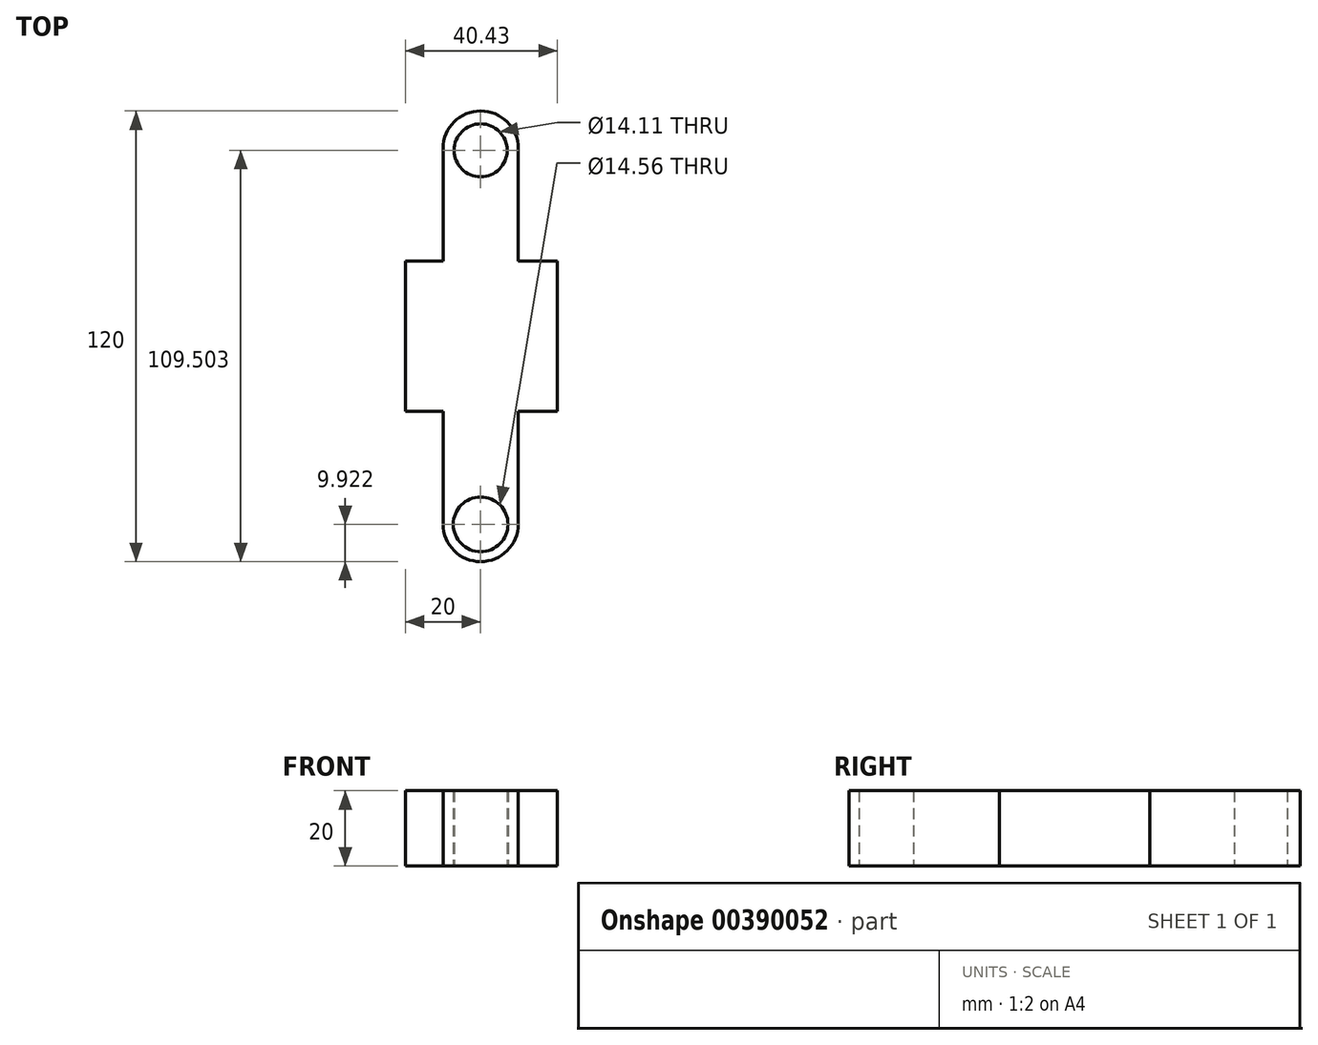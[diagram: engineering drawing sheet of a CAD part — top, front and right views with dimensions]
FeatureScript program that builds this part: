
annotation { "Feature Type Name" : "Feature", "Feature Type Description" : "" }
export const myFeature = defineFeature(function(context is Context, id is Id, definition is map)
    precondition{}
    {
        {
            var Q0;
            Q0=qCreatedBy(makeId("Top.planeOp"),FACE);
            var sketch = newSketch(context, id + "F0", { "sketchPlane" : qUnion([Q0])});
            skLineSegment(sketch, "E0", {"start": v(-20, 0) * mm, "end": v(-20, 20) * mm});
            skLineSegment(sketch, "E1", {"start": v(-20, 20) * mm, "end": v(-10, 20) * mm});
            skLineSegment(sketch, "E2", {"start": v(-10, 20) * mm, "end": v(-10, 60) * mm});
            skLineSegment(sketch, "E3", {"start": v(-10, 60) * mm, "end": v(10, 60) * mm});
            skLineSegment(sketch, "E4", {"start": v(10, 60) * mm, "end": v(10, 20) * mm});
            skLineSegment(sketch, "E5", {"start": v(10, 20) * mm, "end": v(20.43, 20) * mm});
            skLineSegment(sketch, "E6", {"start": v(20.43, 20) * mm, "end": v(20.43, -20) * mm});
            skLineSegment(sketch, "E7", {"start": v(20.43, -20) * mm, "end": v(10, -20) * mm});
            skLineSegment(sketch, "E8", {"start": v(10, -20) * mm, "end": v(10, -60) * mm});
            skLineSegment(sketch, "E9", {"start": v(10, -60) * mm, "end": v(-10, -60) * mm});
            skLineSegment(sketch, "E10", {"start": v(-10, -60) * mm, "end": v(-10, -20) * mm});
            skLineSegment(sketch, "E11", {"start": v(-10, -20) * mm, "end": v(-20, -20) * mm});
            skLineSegment(sketch, "E12", {"start": v(-20, -20) * mm, "end": v(-20, 0) * mm});
            skPoint(sketch, "E13.endSnap0", {"position": v(0, 60) * mm});
            skCircle(sketch, "E14", {"center": v(0, 49.5) * mm, "radius": 7.06 * mm});
            skCircle(sketch, "E15", {"center": v(0, -50.08) * mm, "radius": 7.28 * mm});
            skPoint(sketch, "E13.start.orphan", {"position": v(0, 60) * mm});
            skPoint(sketch, "E16.start.orphan", {"position": v(0, -60) * mm});
            skSolve(sketch);
        }
        {
            var Q0;
            Q0 = qSketchRegion(id + "F0", true);
            var Q1;
            Q1=makeQuery(id+"F0.imprint","IMPRINT",FACE,{"disambiguationData":[TD([[makeQuery(id+"F0.imprint","IMPRINT",EDGE,{"derivedFrom":sQuery(id+"F0.wireOp",EDGE,"E0")}),-1.0]])]});
            extrude(context, id + "F1", {"entities" : qUnion([Q0, Q1]), "depth" : 20 * mm});
        }
        {
            var Q0;
            Q0=makeQuery(id+"F1.opExtrude","SWEPT_EDGE",EDGE,{"disambiguationData":[OSD([sQuery(id+"F0.wireOp",EDGE,"E3"),sQuery(id+"F0.wireOp",EDGE,"E4")])]});
            var Q1;
            Q1=makeQuery(id+"F1.opExtrude","SWEPT_EDGE",EDGE,{"disambiguationData":[OSD([sQuery(id+"F0.wireOp",EDGE,"E2"),sQuery(id+"F0.wireOp",EDGE,"E3")])]});
            var Q2;
            Q2=makeQuery(id+"F1.opExtrude","SWEPT_EDGE",EDGE,{"disambiguationData":[OSD([sQuery(id+"F0.wireOp",EDGE,"E8"),sQuery(id+"F0.wireOp",EDGE,"E9")])]});
            var Q3;
            Q3=makeQuery(id+"F1.opExtrude","SWEPT_EDGE",EDGE,{"disambiguationData":[OSD([sQuery(id+"F0.wireOp",EDGE,"E9"),sQuery(id+"F0.wireOp",EDGE,"E10")])]});
            fillet(context, id + "F2", {"entities" : qUnion([Q0, Q1, Q2, Q3]), "radius" : 10 * mm, "tangentPropagation" : true, "allowEdgeOverflow" : false});
        }
    });
